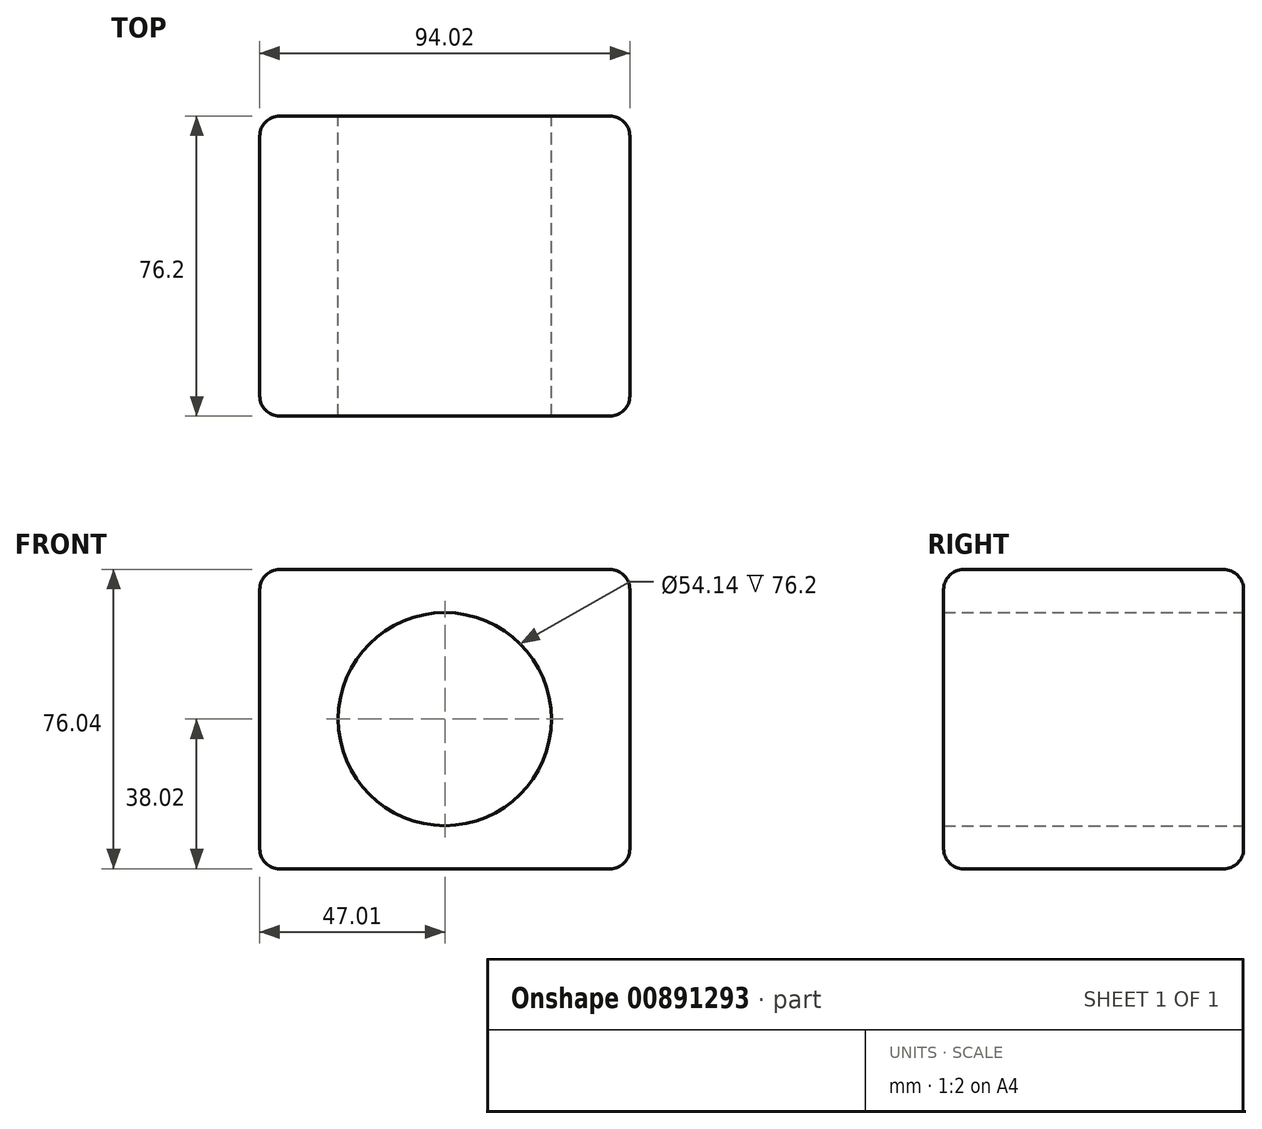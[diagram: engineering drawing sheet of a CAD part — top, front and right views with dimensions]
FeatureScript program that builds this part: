
annotation { "Feature Type Name" : "Feature", "Feature Type Description" : "" }
export const myFeature = defineFeature(function(context is Context, id is Id, definition is map)
    precondition{}
    {
        {
            var Q0;
            Q0=qCreatedBy(makeId("Front.planeOp"),FACE);
            var sketch = newSketch(context, id + "F0", { "sketchPlane" : qUnion([Q0])});
            skLineSegment(sketch, "E0.bottom", {"start": v(47.01, 38.02) * mm, "end": v(-47.01, 38.02) * mm});
            skLineSegment(sketch, "E0.top", {"start": v(47.01, -38.02) * mm, "end": v(-47.01, -38.02) * mm});
            skLineSegment(sketch, "E0.left", {"start": v(47.01, 38.02) * mm, "end": v(47.01, -38.02) * mm});
            skLineSegment(sketch, "E0.right", {"start": v(-47.01, 38.02) * mm, "end": v(-47.01, -38.02) * mm});
            skPoint(sketch, "E0.middle", {"position": v(0, 0) * mm});
            skSolve(sketch);
        }
        {
            var Q0;
            Q0=makeQuery(id+"F0.imprint","IMPRINT",FACE,{"disambiguationData":[TD([[makeQuery(id+"F0.imprint","IMPRINT",EDGE,{"derivedFrom":sQuery(id+"F0.wireOp",EDGE,"E0.bottom")}),1.0]])]});
            extrude(context, id + "F1", {"entities" : qUnion([Q0]), "depth" : 76.2 * mm, "offsetDistance" : 25.4 * mm});
        }
        {
            var Q0;
            Q0=makeQuery(id+"F1.opExtrude","CAP_FACE",FACE,{"disambiguationData":[OSD([sQuery(id+"F0.wireOp",EDGE,"E0.bottom"),sQuery(id+"F0.wireOp",EDGE,"E0.top"),sQuery(id+"F0.wireOp",EDGE,"E0.left"),sQuery(id+"F0.wireOp",EDGE,"E0.right")])],"isStart":true});
            var sketch = newSketch(context, id + "F2", { "sketchPlane" : qUnion([Q0])});
            skCircle(sketch, "E1", {"center": v(0, 0) * mm, "radius": 27.07 * mm});
            skSolve(sketch);
        }
        {
            var Q0;
            Q0=makeQuery(id+"F2.imprint","IMPRINT",FACE,{"disambiguationData":[TD([[makeQuery(id+"F2.imprint","IMPRINT",EDGE,{"derivedFrom":sQuery(id+"F2.wireOp",EDGE,"E1")}),1.0]])]});
            extrude(context, id + "F3", {"entities" : qUnion([Q0]), "operationType" : NewBodyOperationType.REMOVE, "oppositeDirection" : true, "depth" : 101.6 * mm, "offsetDistance" : 25.4 * mm});
        }
        {
            var Q0;
            Q0=makeQuery(id+"F1.opExtrude","CAP_EDGE",EDGE,{"disambiguationData":[OSD([sQuery(id+"F0.wireOp",EDGE,"E0.bottom")])],"isStart":false});
            var Q1;
            Q1=makeQuery(id+"F1.opExtrude","SWEPT_EDGE",EDGE,{"disambiguationData":[OSD([sQuery(id+"F0.wireOp",EDGE,"E0.bottom"),sQuery(id+"F0.wireOp",EDGE,"E0.left")])]});
            var Q2;
            Q2=makeQuery(id+"F1.opExtrude","CAP_EDGE",EDGE,{"disambiguationData":[OSD([sQuery(id+"F0.wireOp",EDGE,"E0.bottom")])],"isStart":true});
            var Q3;
            Q3=makeQuery(id+"F1.opExtrude","SWEPT_EDGE",EDGE,{"disambiguationData":[OSD([sQuery(id+"F0.wireOp",EDGE,"E0.bottom"),sQuery(id+"F0.wireOp",EDGE,"E0.right")])]});
            var Q4;
            Q4=makeQuery(id+"F1.opExtrude","CAP_EDGE",EDGE,{"disambiguationData":[OSD([sQuery(id+"F0.wireOp",EDGE,"E0.left")])],"isStart":false});
            var Q5;
            Q5=makeQuery(id+"F1.opExtrude","CAP_EDGE",EDGE,{"disambiguationData":[OSD([sQuery(id+"F0.wireOp",EDGE,"E0.left")])],"isStart":true});
            var Q6;
            Q6=makeQuery(id+"F1.opExtrude","SWEPT_EDGE",EDGE,{"disambiguationData":[OSD([sQuery(id+"F0.wireOp",EDGE,"E0.top"),sQuery(id+"F0.wireOp",EDGE,"E0.left")])]});
            var Q7;
            Q7=makeQuery(id+"F1.opExtrude","CAP_EDGE",EDGE,{"disambiguationData":[OSD([sQuery(id+"F0.wireOp",EDGE,"E0.top")])],"isStart":false});
            var Q8;
            Q8=makeQuery(id+"F1.opExtrude","CAP_EDGE",EDGE,{"disambiguationData":[OSD([sQuery(id+"F0.wireOp",EDGE,"E0.right")])],"isStart":false});
            fillet(context, id + "F4", {"entities" : qUnion([Q0, Q1, Q2, Q3, Q4, Q5, Q6, Q7, Q8]), "radius" : 5.08 * mm, "tangentPropagation" : true, "allowEdgeOverflow" : false});
        }
        {
            var Q0;
            Q0=makeQuery(id+"F1.opExtrude","CAP_EDGE",EDGE,{"disambiguationData":[OSD([sQuery(id+"F0.wireOp",EDGE,"E0.top")])],"isStart":true});
            var Q1;
            Q1=makeQuery(id+"F1.opExtrude","CAP_EDGE",EDGE,{"disambiguationData":[OSD([sQuery(id+"F0.wireOp",EDGE,"E0.right")])],"isStart":true});
            var Q2;
            Q2=makeQuery(id+"F1.opExtrude","SWEPT_EDGE",EDGE,{"disambiguationData":[OSD([sQuery(id+"F0.wireOp",EDGE,"E0.top"),sQuery(id+"F0.wireOp",EDGE,"E0.right")])]});
            fillet(context, id + "F5", {"entities" : qUnion([Q0, Q1, Q2]), "radius" : 5.08 * mm, "tangentPropagation" : true, "allowEdgeOverflow" : false});
        }
    });
